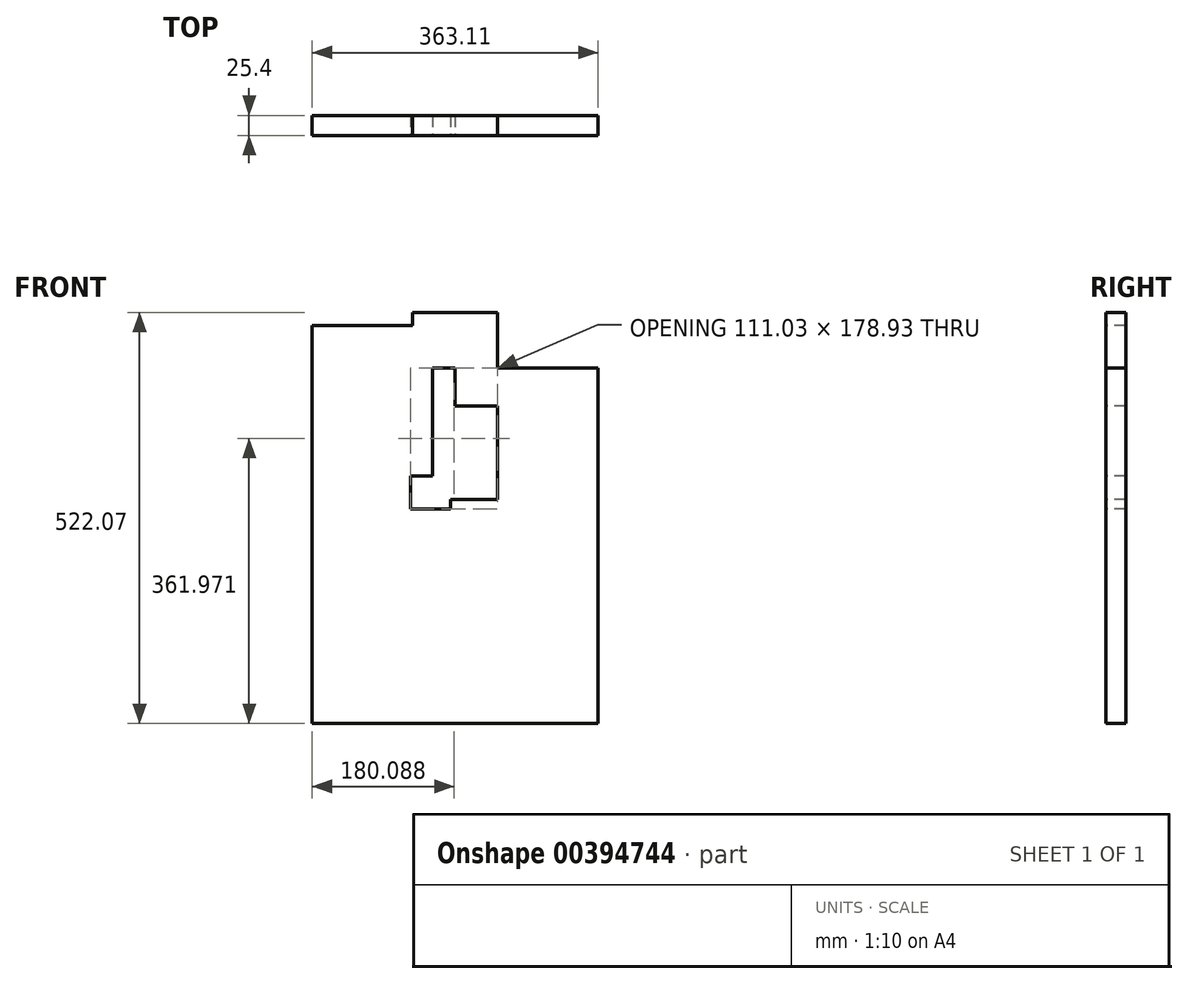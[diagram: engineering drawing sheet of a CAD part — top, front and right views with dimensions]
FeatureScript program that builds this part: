
annotation { "Feature Type Name" : "Feature", "Feature Type Description" : "" }
export const myFeature = defineFeature(function(context is Context, id is Id, definition is map)
    precondition{}
    {
        {
            var Q0;
            Q0=qCreatedBy(makeId("Front.planeOp"),FACE);
            var sketch = newSketch(context, id + "F0", { "sketchPlane" : qUnion([Q0])});
            skLineSegment(sketch, "E0.bottom", {"start": v(-90.78, -191.1) * mm, "end": v(90.78, -191.1) * mm});
            skLineSegment(sketch, "E0.top", {"start": v(-90.78, 191.1) * mm, "end": v(90.78, 191.1) * mm});
            skLineSegment(sketch, "E0.left", {"start": v(-90.78, -191.1) * mm, "end": v(-90.78, 191.1) * mm});
            skLineSegment(sketch, "E0.right", {"start": v(90.78, -191.1) * mm, "end": v(90.78, 191.1) * mm});
            skPoint(sketch, "E0.middle", {"position": v(0, 0) * mm});
            skLineSegment(sketch, "E1.bottom", {"start": v(90.78, -28.67) * mm, "end": v(90.78, -28.67) * mm});
            skLineSegment(sketch, "E1.top", {"start": v(90.78, 118.66) * mm, "end": v(90.78, 118.66) * mm});
            skLineSegment(sketch, "E1.left", {"start": v(90.78, -28.67) * mm, "end": v(90.78, 118.66) * mm});
            skLineSegment(sketch, "E1.right", {"start": v(90.78, -28.67) * mm, "end": v(90.78, 118.66) * mm});
            skPoint(sketch, "E1.middle", {"position": v(90.78, 45) * mm});
            skLineSegment(sketch, "E2.bottom", {"start": v(-90.78, 88.78) * mm, "end": v(272.33, 88.78) * mm});
            skLineSegment(sketch, "E2.top", {"start": v(-90.78, -88.78) * mm, "end": v(272.33, -88.78) * mm});
            skLineSegment(sketch, "E2.left", {"start": v(-90.78, 88.78) * mm, "end": v(-90.78, -88.78) * mm});
            skLineSegment(sketch, "E2.right", {"start": v(272.33, 88.78) * mm, "end": v(272.33, -88.78) * mm});
            skPoint(sketch, "E2.middle", {"position": v(90.78, 0) * mm});
            skLineSegment(sketch, "E3.bottom", {"start": v(144.82, -30.01) * mm, "end": v(36.73, -30.01) * mm});
            skLineSegment(sketch, "E3.top", {"start": v(144.82, 207.57) * mm, "end": v(36.73, 207.57) * mm});
            skLineSegment(sketch, "E3.left", {"start": v(144.82, -30.01) * mm, "end": v(144.82, 207.57) * mm});
            skLineSegment(sketch, "E3.right", {"start": v(36.73, -30.01) * mm, "end": v(36.73, 207.57) * mm});
            skPoint(sketch, "E3.middle", {"position": v(90.78, 88.78) * mm});
            skLineSegment(sketch, "E4.bottom", {"start": v(272.33, 136.94) * mm, "end": v(-90.78, 136.94) * mm});
            skLineSegment(sketch, "E4.top", {"start": v(272.33, -314.5) * mm, "end": v(-90.78, -314.5) * mm});
            skLineSegment(sketch, "E4.left", {"start": v(272.33, 136.94) * mm, "end": v(272.33, -314.5) * mm});
            skLineSegment(sketch, "E4.right", {"start": v(-90.78, 136.94) * mm, "end": v(-90.78, -314.5) * mm});
            skPoint(sketch, "E4.middle", {"position": v(90.78, -88.78) * mm});
            skLineSegment(sketch, "E5.bottom", {"start": v(-9.59, 0) * mm, "end": v(191.14, 0) * mm});
            skLineSegment(sketch, "E5.top", {"start": v(-9.59, 0) * mm, "end": v(191.14, 0) * mm});
            skLineSegment(sketch, "E5.left", {"start": v(-9.59, 0) * mm, "end": v(-9.59, 0) * mm});
            skLineSegment(sketch, "E5.right", {"start": v(191.14, 0) * mm, "end": v(191.14, 0) * mm});
            skLineSegment(sketch, "E6.bottom", {"start": v(90.78, -28.67) * mm, "end": v(91.88, -28.67) * mm});
            skLineSegment(sketch, "E6.top", {"start": v(90.78, 17.86) * mm, "end": v(91.88, 17.86) * mm});
            skLineSegment(sketch, "E6.left", {"start": v(90.78, -28.67) * mm, "end": v(90.78, 17.86) * mm});
            skLineSegment(sketch, "E6.right", {"start": v(91.88, -28.67) * mm, "end": v(91.88, 17.86) * mm});
            skPoint(sketch, "E6.middle", {"position": v(91.33, -5.4) * mm});
            skLineSegment(sketch, "E7.bottom", {"start": v(44.02, -30.01) * mm, "end": v(74.73, -30.01) * mm});
            skLineSegment(sketch, "E7.top", {"start": v(44.02, -11.98) * mm, "end": v(74.73, -11.98) * mm});
            skLineSegment(sketch, "E7.left", {"start": v(44.02, -30.01) * mm, "end": v(44.02, -11.98) * mm});
            skLineSegment(sketch, "E7.right", {"start": v(74.73, -30.01) * mm, "end": v(74.73, -11.98) * mm});
            skPoint(sketch, "E7.middle", {"position": v(59.38, -21) * mm});
            skLineSegment(sketch, "E8.bottom", {"start": v(84.96, 0) * mm, "end": v(33.8, 0) * mm});
            skLineSegment(sketch, "E8.top", {"start": v(84.96, -42) * mm, "end": v(33.8, -42) * mm});
            skLineSegment(sketch, "E8.left", {"start": v(84.96, 0) * mm, "end": v(84.96, -42) * mm});
            skLineSegment(sketch, "E8.right", {"start": v(33.8, 0) * mm, "end": v(33.8, -42) * mm});
            skSolve(sketch);
        }
        {
            var Q0;
            Q0 = qSketchRegion(id + "F0", true);
            extrude(context, id + "F1", {"entities" : qUnion([Q0]), "oppositeDirection" : true, "depth" : 25.4 * mm});
        }
        {
            var Q0;
            {var subQ0=sQuery(id+"F0.wireOp",EDGE,"E3.right");var subQ1=makeQuery(id+"F0.imprint","INTERSECT",VERTEX,{"derivedFrom":[sQuery(id+"F0.wireOp",EDGE,"E2.bottom"),subQ0]});Q0=makeQuery(id+"F1.opExtrude","SWEPT_FACE",FACE,{"disambiguationData":[OSD([subQ0]),TDD([makeQuery(id+"F0.imprint","IMPRINT",EDGE,{"disambiguationData":[TD([[subQ1,1.0]])],"derivedFrom":subQ0}),makeQuery(id+"F0.imprint","IMPRINT",EDGE,{"disambiguationData":[TD([[subQ1,-1.0]])],"derivedFrom":subQ0})])]});}
            extrude(context, id + "F2", {"entities" : qUnion([Q0]), "operationType" : NewBodyOperationType.ADD, "depth" : 25.4 * mm});
        }
    });
